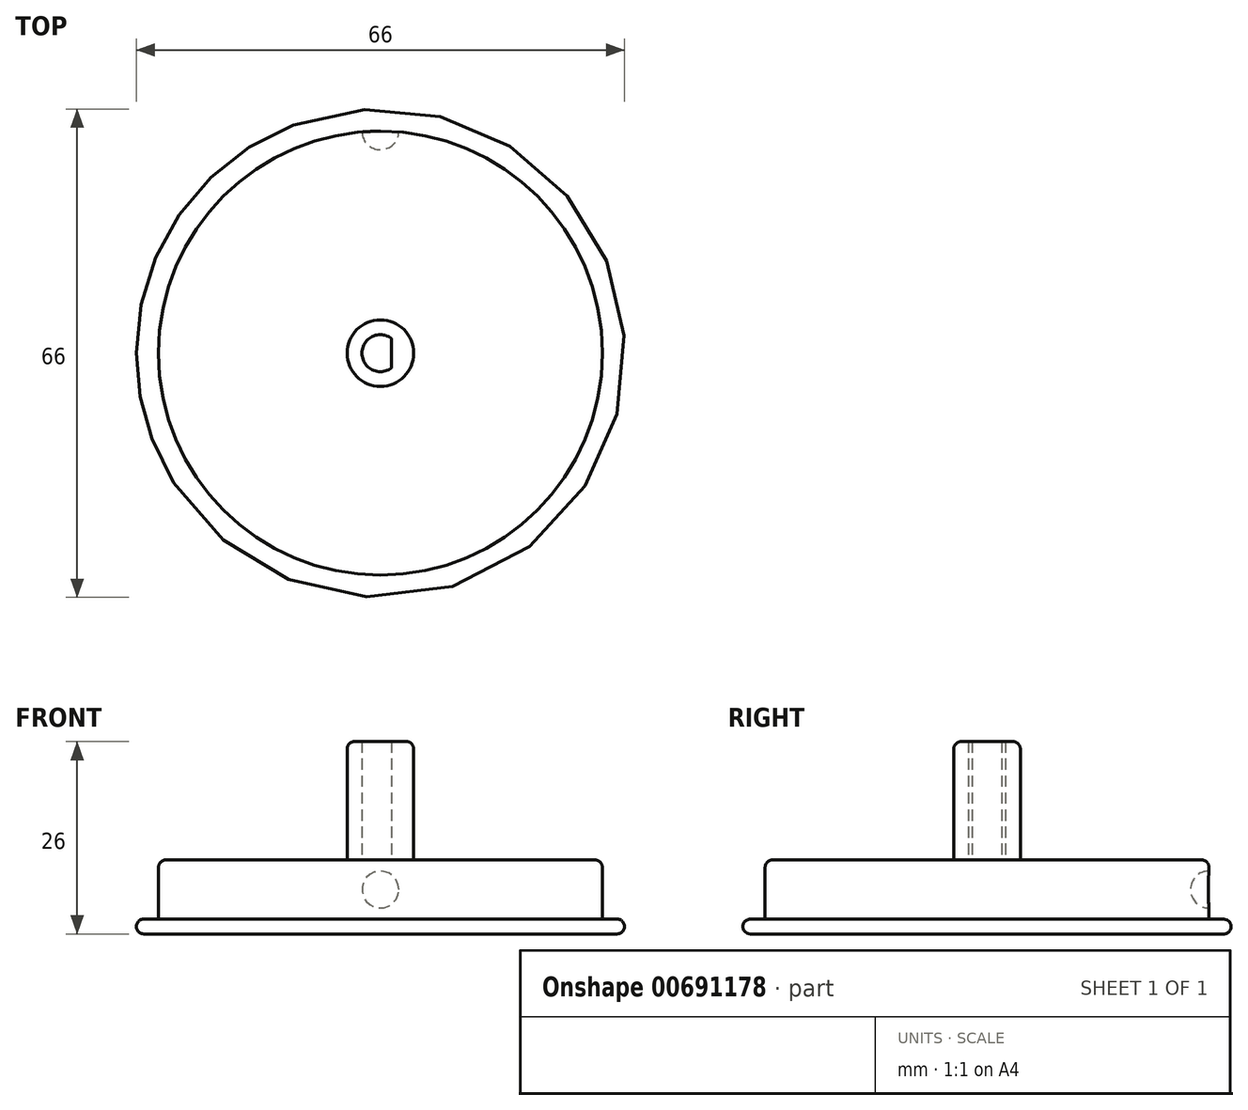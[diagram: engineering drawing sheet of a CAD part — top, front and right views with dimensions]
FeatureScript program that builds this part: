
annotation { "Feature Type Name" : "Feature", "Feature Type Description" : "" }
export const myFeature = defineFeature(function(context is Context, id is Id, definition is map)
    precondition{}
    {
        {
            var Q0;
            Q0=qCreatedBy(makeId("Top.planeOp"),FACE);
            var sketch = newSketch(context, id + "F0", { "sketchPlane" : qUnion([Q0])});
            skCircle(sketch, "E0", {"center": v(0, 0) * mm, "radius": 30 * mm});
            skCircle(sketch, "E1", {"center": v(0, 0) * mm, "radius": 4.5 * mm});
            skArc(sketch, "E2", {"start": v(1.5, 2) * mm, "mid": v(-2.5, 0) * mm, "end": v(1.5, -2) * mm});
            skLineSegment(sketch, "E3", {"start": v(1.5, 2) * mm, "end": v(1.5, -2) * mm});
            skSolve(sketch);
        }
        {
            var Q0;
            Q0 = qSketchRegion(id + "F0", true);
            var Q1;
            Q1=makeQuery(id+"F0.imprint","IMPRINT",FACE,{"disambiguationData":[TD([[makeQuery(id+"F0.imprint","IMPRINT",EDGE,{"derivedFrom":sQuery(id+"F0.wireOp",EDGE,"E1")}),1.0]])]});
            var Q2;
            Q2=makeQuery(id+"F0.imprint","IMPRINT",FACE,{"disambiguationData":[TD([[makeQuery(id+"F0.imprint","IMPRINT",EDGE,{"derivedFrom":sQuery(id+"F0.wireOp",EDGE,"E2")}),1.0]])]});
            extrude(context, id + "F1", {"entities" : qUnion([Q0, Q1, Q2]), "endBound" : BoundingType.SYMMETRIC, "depth" : 8 * mm, "offsetDistance" : 25 * mm});
        }
        {
            var Q0;
            Q0=makeQuery(id+"F0.imprint","IMPRINT",FACE,{"disambiguationData":[TD([[makeQuery(id+"F0.imprint","IMPRINT",EDGE,{"derivedFrom":sQuery(id+"F0.wireOp",EDGE,"E1")}),1.0]])]});
            extrude(context, id + "F2", {"entities" : qUnion([Q0]), "operationType" : NewBodyOperationType.ADD, "depth" : 20 * mm, "offsetDistance" : 25 * mm});
        }
        {
            var Q0;
            Q0=qCreatedBy(makeId("Top.planeOp"),FACE);
            var sketch = newSketch(context, id + "F3", { "sketchPlane" : qUnion([Q0])});
            skArc(sketch, "E4", {"start": v(-2.5, 30) * mm, "mid": v(0, 27.5) * mm, "end": v(2.5, 30) * mm});
            skLineSegment(sketch, "E5", {"start": v(2.5, 30) * mm, "end": v(-2.5, 30) * mm});
            skSolve(sketch);
        }
        {
            var Q0;
            Q0 = qSketchRegion(id + "F3", true);
            var Q1;
            Q1=sQuery(id+"F3.wireOp",EDGE,"E5");
            revolve(context, id + "F4", {"operationType" : NewBodyOperationType.REMOVE, "entities" : qUnion([Q0]), "axis" : qUnion([Q1]), "revolveType" : RevolveType.FULL, "oppositeDirection" : true});
        }
        {
            var Q0;
            Q0=makeQuery(id+"F1.opExtrude","CAP_FACE",FACE,{"disambiguationData":[OSD([sQuery(id+"F0.wireOp",EDGE,"E0")])],"isStart":true});
            var sketch = newSketch(context, id + "F5", { "sketchPlane" : qUnion([Q0])});
            skCircle(sketch, "E6", {"center": v(0, 0) * mm, "radius": 33 * mm});
            skSolve(sketch);
        }
        {
            var Q0;
            Q0 = qSketchRegion(id + "F5", true);
            extrude(context, id + "F6", {"entities" : qUnion([Q0]), "operationType" : NewBodyOperationType.ADD, "depth" : 2 * mm, "offsetDistance" : 25 * mm});
        }
        {
            var Q0;
            Q0=makeQuery(id+"FzU8lrhnyTqKGNA_1.1.F6.opExtrude","CAP_EDGE",EDGE,{"disambiguationData":[OSD([sQuery(id+"F5.wireOp",EDGE,"E6")])],"isStart":false});
            var Q1;
            Q1=makeQuery(id+"FzU8lrhnyTqKGNA_1.1.F6.opExtrude","CAP_EDGE",EDGE,{"disambiguationData":[OSD([sQuery(id+"F5.wireOp",EDGE,"E6")])],"isStart":true});
            var Q2;
            Q2=makeQuery(id+"F1.opExtrude","CAP_EDGE",EDGE,{"disambiguationData":[OSD([sQuery(id+"F0.wireOp",EDGE,"E0")])],"isStart":false});
            var Q3;
            Q3=makeQuery(id+"F1.opExtrude","CAP_EDGE",EDGE,{"disambiguationData":[OSD([sQuery(id+"F0.wireOp",EDGE,"E0")])],"isStart":true});
            var Q4;
            Q4=makeQuery(id+"F6.opExtrude","CAP_EDGE",EDGE,{"disambiguationData":[OSD([sQuery(id+"F5.wireOp",EDGE,"E6")])],"isStart":true});
            var Q5;
            Q5=makeQuery(id+"F6.opExtrude","CAP_EDGE",EDGE,{"disambiguationData":[OSD([sQuery(id+"F5.wireOp",EDGE,"E6")])],"isStart":false});
            var Q6;
            Q6=makeQuery(id+"FzU8lrhnyTqKGNA_1.1.F6.boolean.opBoolean","INTERSECT",EDGE,{"derivedFrom":[makeQuery(id+"F2.opExtrude","SWEPT_FACE",FACE,{"disambiguationData":[OSD([sQuery(id+"F0.wireOp",EDGE,"E1")])]}),makeQuery(id+"FzU8lrhnyTqKGNA_1.1.F6.opExtrude","CAP_FACE",FACE,{"disambiguationData":[OSD([sQuery(id+"F5.wireOp",EDGE,"E6")])],"isStart":false})]});
            var Q7;
            Q7=makeQuery(id+"F2.opExtrude","CAP_EDGE",EDGE,{"disambiguationData":[OSD([sQuery(id+"F0.wireOp",EDGE,"E1")])],"isStart":false});
            fillet(context, id + "F7", {"entities" : qUnion([Q0, Q1, Q2, Q3, Q4, Q5, Q6, Q7]), "radius" : 1 * mm, "tangentPropagation" : true, "allowEdgeOverflow" : false});
        }
    });
